AUTODESK INVENTOR PART (.ipt)
format: ipt  version: 2016 (Build 200138000, 138)  size: 591,360 bytes
history: native  units: mm (DEFAULTED — no unit token found)
features: other x50, plane x15, sketch x15, sweep x15
ambient origin geometry x8: Origin, YZ Plane, XZ Plane, XY Plane, X Axis, Y Axis, Z Axis, Center Point
bodies: Body1 (feature_tree), Body2 (feature_tree), Body3 (feature_tree), Body4 (feature_tree), Body5 (feature_tree), Body6 (feature_tree), Body7 (feature_tree), Body8 (feature_tree), Body9 (feature_tree), Body10 (feature_tree), Body11 (feature_tree), Body12 (feature_tree), Body13 (feature_tree), Body14 (feature_tree), Body15 (feature_tree)
feature tree (95):
  other  "Work Point1"
  other  "Work Point2"
  other  "Wire1"
  other  "Work Point3"
  other  "Work Point4"
  other  "Wire2"
  other  "Work Point5"
  other  "Work Point6"
  other  "Wire3"
  other  "Work Point7"
  other  "Work Point8"
  other  "Wire4"
  other  "Work Point9"
  other  "Work Point10"
  other  "Wire5"
  other  "Work Point11"
  other  "Work Point12"
  other  "Wire6"
  other  "Work Point13"
  other  "Work Point14"
  other  "Wire7"
  other  "Work Point15"
  other  "Work Point16"
  other  "Segment1"
  other  "Work Point17"
  plane  "Work Plane8"
  plane  "Work Plane9"
  plane  "Work Plane10"
  plane  "Work Plane11"
  plane  "Work Plane12"
  plane  "Work Plane13"
  plane  "Work Plane14"
  plane  "Work Plane15"
  plane  "Work Plane16"
  plane  "Work Plane17"
  plane  "Work Plane18"
  plane  "Work Plane19"
  plane  "Work Plane20"
  plane  "Work Plane21"
  plane  "Work Plane22"
  other  "Work Point18"
  other  "Work Point19"
  other  "Work Point20"
  other  "Work Point21"
  other  "Work Point22"
  other  "Work Point23"
  other  "Work Point24"
  other  "Work Point25"
  other  "Work Point26"
  other  "Work Point27"
  sketch  "Sketch8"  dims[d14=0.0mm d15=0.0mm d16=0.0mm d17=0.0mm]
  other  "Srf8"
  sketch  "Sketch9"  dims[d18=0.0mm d19=0.0mm d20=0.0mm d21=0.0mm]
  other  "Srf9"
  sketch  "Sketch10"  dims[d22=0.0mm d23=0.0mm d24=0.0mm d25=0.0mm]
  other  "Srf10"
  sketch  "Sketch11"  dims[d26=0.0mm d27=0.0mm d28=0.0mm d29=0.0mm]
  other  "Srf11"
  sketch  "Sketch12"  dims[d30=0.0mm d31=0.0mm d32=0.0mm d33=0.0mm]
  other  "Srf12"
  sketch  "Sketch13"  dims[d34=0.0mm d35=0.0mm d36=0.0mm d37=0.0mm]
  other  "Srf13"
  sketch  "Sketch14"  dims[d38=0.0mm d39=0.0mm d40=0.0mm d41=0.0mm]
  other  "Srf14"
  sketch  "Sketch15"  dims[d42=0.0mm d43=0.0mm]
  other  "Srf15"
  sketch  "Sketch16"
  other  "Srf16"
  sketch  "Sketch17"
  other  "Srf17"
  sketch  "Sketch18"
  other  "Srf18"
  sketch  "Sketch19"
  other  "Srf19"
  sketch  "Sketch20"
  other  "Srf20"
  sketch  "Sketch21"
  other  "Srf21"
  sketch  "Sketch22"
  other  "Srf22"
  sweep  "SweepSrf8"
  sweep  "SweepSrf9"
  sweep  "SweepSrf10"
  sweep  "SweepSrf11"
  sweep  "SweepSrf12"
  sweep  "SweepSrf13"
  sweep  "SweepSrf14"
  sweep  "SweepSrf15"
  sweep  "SweepSrf16"
  sweep  "SweepSrf17"
  sweep  "SweepSrf18"
  sweep  "SweepSrf19"
  sweep  "SweepSrf20"
  sweep  "SweepSrf21"
  sweep  "SweepSrf22"
